# Revit family: Access_Panel-Wall_Door-Activar-Heavy_Duty-Interior_Access-FD
name_source: partatom
category: Doors
revit_build: Autodesk Revit MEP 2012 (Build: 20110309_2315(x64)
units: mm (PartAtom-declared; Revit-internal decimal feet)

## types (1)
- Access_Panel-Wall_Door-Activar-Heavy_Duty-Interior_Access-FD
    04 CSI = 08 31 16
    95 CSI = 08310
    Additional Info URL = http://www.activarcpg.com
    Anchors Available = Masonry Anchors Standard
    Assembly Code = C1020700
    CSFM = This product has been approved by the California State Fire Marshall (CSFM) pursuant to Section 13144.1 of the California Health and Safety Code. See CSFM Listing No 3330-1223:101 for allowable values and/or conditions for use concerning material presented in this document. It is subject reexamination, revision and possible cancellation.
    Color Availability = Red (R), Black (BK), Flat Black (FB), Sand (S), AMS Beige (AB), SC Flat Beige (SB), Gray (G), Bronze (B), Silver (SI)
    Custom Size Note = Custom sizes are available.  Contact manufacturer for availability.
    Default Elevation = 48"
    Description = Fire-Rated & Insulated Flush Frame Access Panel
    Door = 2” thick, insulated 14 gauge steel with continuous hinge.
    Drywall Bead Installation = Yes
    Fire Rating Wall Installation = 1-1/2 hour UL“B” label in a 2 hour fire barrier. File # R13067-1. Maximum size 48” x 48”. HGFD max wall size 24" x 48"
    Frame = 14 gauge steel with a 1” flange. Welded-on masonry anchor.
    Hardware = Universal turn ring and key lock (U).
    Height = 10"
    Maitenance URL = http://www.activarcpg.com
    Manufacturer = Activar Construction Products Group
    Manufacturer Fax = 952-835-2218
    Model = FD-0808UW-H16
    Number of Latches = 1
    Opening Gap = 3/16"
    Options = Additional Colors, Galvanized Finish, Mortise Slam Lock Prep (U3) or Mortise Slam Lock Installed (U4).
    Panel Type Use = Heavy Gauge and Security (Wall Only - Sizes Up to 24x48)
    Product Line = Fire-Rated Access Panels
    Product Page URL = http://www.activarcpg.com
    Rough Height = 8 3/8"
    Rough Width = 8 3/8"
    Shipping Weight = 11.00 lb
    Subcategory = Access Panels
    Submittal URL = http://www.activarcpg.com
    URL = http://www.activarcpg.com
    Warranty URL = http://www.activarcpg.com
    Width = 10"
    ecoScorecard Product Page = http://ecoscorecard.com

## geometry (parser evidence)
native form markers: Blend x4, Sweep x3
no freeform markers — native parametric forms only
